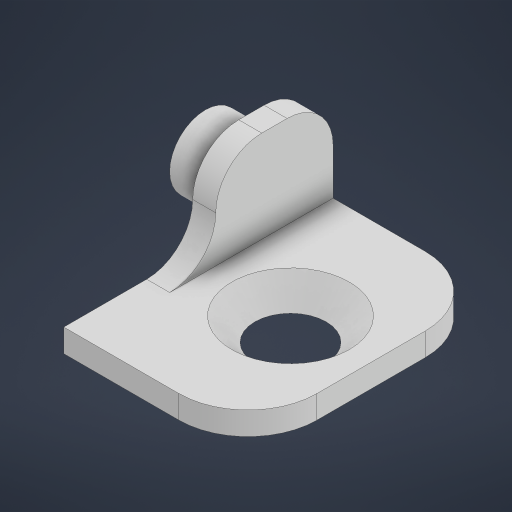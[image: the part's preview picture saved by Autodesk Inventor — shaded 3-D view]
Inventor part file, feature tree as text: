
AUTODESK INVENTOR PART (.ipt)
format: ipt  version: 2024 (Build 280153000, 153)  size: 245,248 bytes
history: native  units: in
note: dims shown in document units (in); Inventor stores cm internally (conversion verified against a paired STEP export)
features: sketch x4, extrude x3, fillet x3, hole x1, chamfer x1
ambient origin geometry x8: Origin, YZ Plane, XZ Plane, XY Plane, X Axis, Y Axis, Z Axis, Center Point
bodies: Solid1 (feature_tree)
feature tree (12):
  extrude  "Extrusion1"  Depth=0.1969in
  extrude  "Extrusion2"  Depth=0.4213in TaperAngle=0.0deg
  hole  "Hole1"  [1 undecoded]
  fillet  "Fillet1"  Radius=0.0394in
  fillet  "Fillet3"  Radius=0.0787in
  extrude  "Extrusion4"  Depth=0.2756in
  fillet  "Fillet4"  Radius=0.1181in
  chamfer  "Chamfer2"  Distance=0.1004in
  sketch  "Sketch1"  dims[d0=0.315in d1=0.1969in]
  sketch  "Sketch2"  dims[d2=0.0394in d3=0.4213in d4=0.0in]
  sketch  "Sketch3"  dims[d5=0.122in d6=0.1004in d8=0.0394in d9=0.0787in d10=0.0in]
  sketch  "Sketch5"  dims[d11=0.1378in d12=0.2106in d13=0.122in d14=0.2362in d15=0.1575in d16=0.0787in d17=90.0deg d18=0.315in d19=0.8108in d21=0.1181in d28=0.1004in d30=0.0787in d31=0.1575in d32=0.1004in d33=0.0394in d34=0.0in d35=0.0787in d36=0.0394in d37=0.2756in d38=45.0deg d22=0.0344in d23=0.0197in d24=0.0344in]
note: 1 required parameter value undecoded (feature->parameter linkage not recoverable at this tier; creation-order binding heuristic only, values carry confidence <= 0.55)
